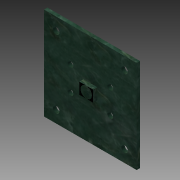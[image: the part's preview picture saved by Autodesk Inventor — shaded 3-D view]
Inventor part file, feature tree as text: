
AUTODESK INVENTOR PART (.ipt)
format: ipt  version: 2014 (Build 180170000, 170)  size: 147,456 bytes
history: native  units: in
note: dims shown in document units (in); Inventor stores cm internally (conversion verified against a paired STEP export)
features: extrude x4, sketch x4
ambient origin geometry x8: Origin, YZ Plane, XZ Plane, XY Plane, X Axis, Y Axis, Z Axis, Center Point
bodies: Solid1 (feature_tree)
feature tree (8):
  extrude  "Extrusion1"  Depth=1.657in
  extrude  "Extrusion2"  Depth=0.062in
  extrude  "Extrusion3"  Depth=1.105in
  extrude  "Extrusion4"  Depth=0.001in
  sketch  "Sketch1"  dims[d0=1.657in d1=1.657in]
  sketch  "Sketch2"  dims[d2=0.062in d3=0.0in d4=0.1181in]
  sketch  "Sketch3"  dims[d5=0.102in d6=1.105in]
  sketch  "Sketch4"  dims[d7=0.1579in d8=0.1579in d9=1.105in d10=0.1579in d11=0.609in d12=0.335in d13=0.422in d14=0.422in d15=0.559in d16=0.559in d17=0.062in d18=0.0in d19=0.248in d20=0.203in d21=0.727in d22=0.727in d23=0.7045in d24=0.7045in d25=0.074in d26=0.0in d27=0.124in d28=0.124in d29=0.001in d30=0.0in]
